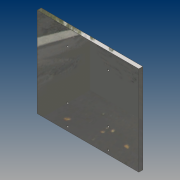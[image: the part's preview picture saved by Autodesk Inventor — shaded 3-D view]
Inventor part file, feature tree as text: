
AUTODESK INVENTOR PART (.ipt)
format: ipt  version: 2021 (Build 250183000, 183)  size: 134,656 bytes
history: native  units: mm
features: reference x9, other x6, sketch x3, extrude x2, hole x1
ambient origin geometry x8: Origin, YZ Plane, XZ Plane, XY Plane, X Axis, Y Axis, Z Axis, Center Point
bodies: Solid1 (feature_tree)
feature tree (21):
  extrude  "Extrusion1"  Depth=250.0mm
  hole  "Hole1"  [1 undecoded]
  extrude  "Extrusion2"  Depth=10.0mm
  sketch  "Sketch1"  dims[d0=220.0mm d1=250.0mm]
  sketch  "Sketch2"  dims[d2=10.0mm d3=0.0mm d4=75.0mm]
  sketch  "Sketch3"  dims[d5=10.0mm d6=50.0mm d7=30.0mm d8=4.5mm d9=6.0mm d10=4.0mm d11=2.0mm d12=90.0deg d13=8.0mm d14=20.594885mm d15=10.0mm d16=0.0mm]
  reference  "Reference1"
  reference  "Reference2"
  reference  "Reference3"
  reference  "Reference4"
  reference  "Reference5"
  reference  "Reference6"
  reference  "Reference7"
  reference  "Reference8"
  reference  "Reference9"
  other  "0002_Tam_nguyen_Truc_Z.iam"
  other  "SK10:2"
  other  "0002_Truc_Z:1"
  other  "Goi_do_B:1"
  other  "SK10:1"
  other  "Goi_do_A:1"
note: 1 required parameter value undecoded (feature->parameter linkage not recoverable at this tier; creation-order binding heuristic only, values carry confidence <= 0.55)
